# Revit family: Valve-Safety_Shutoff-Cla_Val-50_33-Threaded-SI--
name_source: partatom
category: Pipe Accessories
units: mm (PartAtom-declared; Revit-internal decimal feet)

## family parameters
Always vertical = Yes
Cut with Voids When Loaded = No
Part Type = Valve - Breaks Into
Round Connector Dimension = Use Diameter
Shared = No
Work Plane-Based = No

## types (1)
- ERROR_LOAD TYPE CATALOG
    Arrow Height = 30 mm
    Arrow Length = 45 mm
    Assembly Code = D2090
    Axis to Arrow = 134 mm
    Body Material = Metal - CLA-VAL - Ductile Iron - Blue
    CV (liters per second) = 2
    Connection Axis to Valve Top = 140 mm
    Connection End Length = 14 mm
    Connection Radius = 20 mm
    Connection Size = 40 mm
    Connection Type = Threaded
    Connection to Connection = 179 mm
    Control Tube Line Size Diameter = 6 mm
    Control Tube Line Size Radius = 3 mm
    Cover Port Center Offset = 26 mm
    Cover Upper Flange Diameter = 143 mm
    Default Elevation = 0 mm
    Description = Safety Shutoff Valve
    ENGworks Global = http://www.ENGworksGlobal.com
    Flow Configuration = In/Out
    K Coefficient = 5.9
    K Coefficient Table = Globe Valve Flanged
    Loss Method = K Coefficient
    Manufacturer = Cla-Val
    Maximum Flow Rate = 7.9 L/s
    Maximum Flow Rate Value = 7.89
    Maximum Operating Temperature = 82 °C
    Maximum Working Pressure = 28 bar
    Minimum Flow Rate = 0.0 L/s
    Minimum Flow Rate Value = 0
    Minimum Operating Temperature = -40 °C
    Model = 50-33
    Overall Length = 216 mm
    Pilot Line Angle Offset = 63 mm
    Pilot Line Height Offset = 21 mm
    Pilot System Offset = 86 mm
    Pipe Plug Circumscribe Length = 6 mm
    Product Page URL = https://www.cla-val.com
    Series = Safety Shutoff Valve
    Side Port Outside Diameter = 12 mm
    Side Ports Offset from Flange = 45 mm
    Standards = ASTM A536 B16.42
    Threaded End Insertion Length = 18 mm
    Threaded Inside Diameter = 47 mm
    Threaded Inside Radius = 23 mm
    Threaded Outside Radius = 28 mm
    Tick Size = 103 mm
    URL = https://www.cla-val.com
    Unit Weight = 7 kgf
    Version = 1
    X Pilot System Offset = 279 mm
    Y Pilot System Offset = 229 mm
    Z Pilot System Offset = 229 mm

## geometry (parser evidence)
native form markers: Sweep x9
no freeform markers — native parametric forms only
